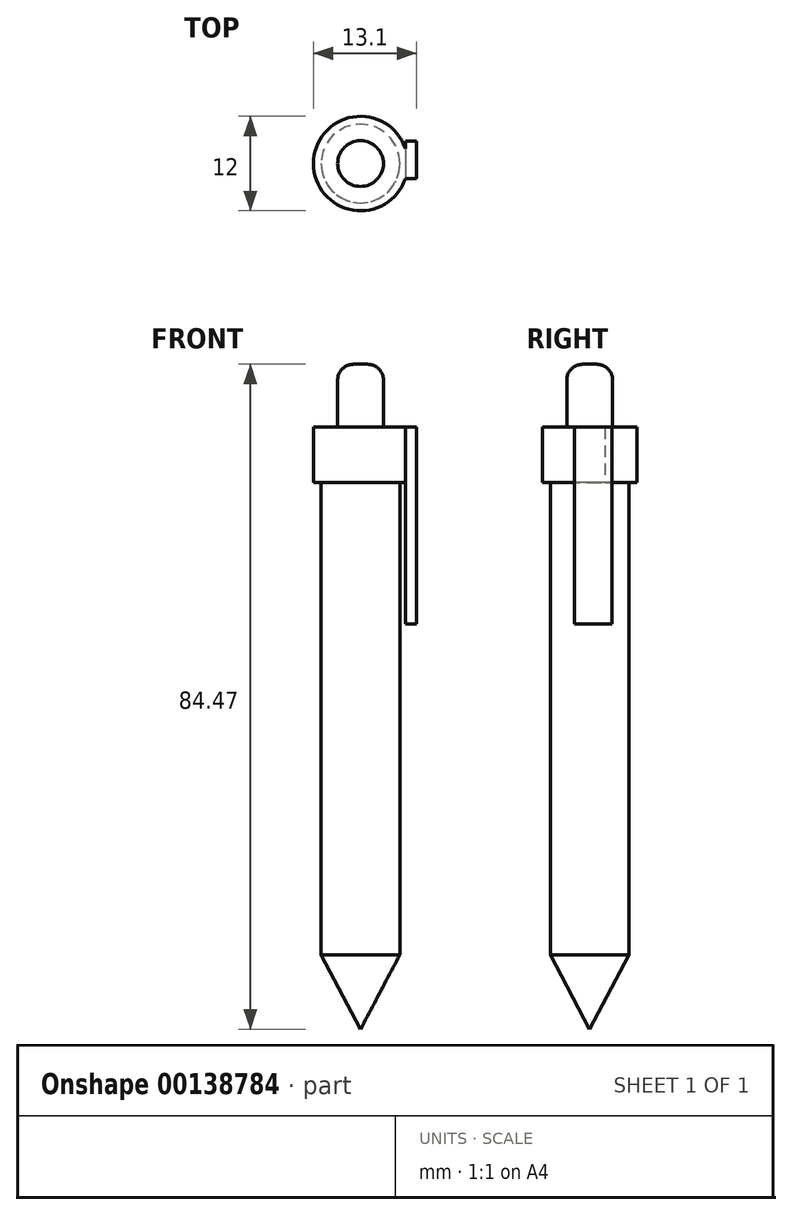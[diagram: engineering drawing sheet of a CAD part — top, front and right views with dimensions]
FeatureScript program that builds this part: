
annotation { "Feature Type Name" : "Feature", "Feature Type Description" : "" }
export const myFeature = defineFeature(function(context is Context, id is Id, definition is map)
    precondition{}
    {
        {
            var Q0;
            Q0=qCreatedBy(makeId("Top.planeOp"),FACE);
            var sketch = newSketch(context, id + "F0", { "sketchPlane" : qUnion([Q0])});
            skCircle(sketch, "E0", {"center": v(0, 0) * mm, "radius": 5 * mm});
            skSolve(sketch);
        }
        {
            var Q0;
            Q0 = qSketchRegion(id + "F0", true);
            extrude(context, id + "F1", {"entities" : qUnion([Q0]), "depth" : 60 * mm});
        }
        {
            var Q0;
            Q0=qCreatedBy(makeId("Right.planeOp"),FACE);
            var sketch = newSketch(context, id + "F2", { "sketchPlane" : qUnion([Q0])});
            skLineSegment(sketch, "E1", {"start": v(0, 0) * mm, "end": v(-5, 0) * mm});
            skLineSegment(sketch, "E2", {"start": v(-5, 0) * mm, "end": v(0, -9.47) * mm});
            skLineSegment(sketch, "E3", {"start": v(0, -9.47) * mm, "end": v(0, 0) * mm});
            skSolve(sketch);
        }
        {
            var Q0;
            Q0 = qSketchRegion(id + "F2", true);
            var Q1;
            Q1=sQuery(id+"F2.wireOp",EDGE,"E3");
            revolve(context, id + "F3", {"entities" : qUnion([Q0]), "axis" : qUnion([Q1]), "revolveType" : RevolveType.FULL});
        }
        {
            var Q0;
            Q0=makeQuery(id+"F1.opExtrude","CAP_FACE",FACE,{"disambiguationData":[OSD([sQuery(id+"F0.wireOp",EDGE,"E0")])],"isStart":false});
            var sketch = newSketch(context, id + "F4", { "sketchPlane" : qUnion([Q0])});
            skCircle(sketch, "E4", {"center": v(0, 0) * mm, "radius": 6 * mm});
            skSolve(sketch);
        }
        {
            var Q0;
            Q0 = qSketchRegion(id + "F4", true);
            extrude(context, id + "F5", {"entities" : qUnion([Q0]), "depth" : 7 * mm});
        }
        {
            var Q0;
            Q0=makeQuery(id+"F5.opExtrude","CAP_FACE",FACE,{"disambiguationData":[OSD([sQuery(id+"F4.wireOp",EDGE,"E4")])],"isStart":false});
            var sketch = newSketch(context, id + "F6", { "sketchPlane" : qUnion([Q0])});
            skLineSegment(sketch, "E5.bottom", {"start": v(7.1, 2.85) * mm, "end": v(5.68, 2.85) * mm});
            skLineSegment(sketch, "E5.top", {"start": v(7.1, -1.92) * mm, "end": v(5.68, -1.92) * mm});
            skLineSegment(sketch, "E5.left", {"start": v(7.1, 2.85) * mm, "end": v(7.1, -1.92) * mm});
            skLineSegment(sketch, "E5.right", {"start": v(5.68, 2.85) * mm, "end": v(5.68, -1.92) * mm});
            skSolve(sketch);
        }
        {
            var Q0;
            Q0 = qSketchRegion(id + "F6", true);
            extrude(context, id + "F7", {"entities" : qUnion([Q0]), "operationType" : NewBodyOperationType.ADD, "oppositeDirection" : true, "depth" : 25 * mm});
        }
        {
            var Q0;
            Q0=makeQuery(id+"F7.boolean.opBoolean","MERGE",FACE,{"derivedFrom":[makeQuery(id+"F5.opExtrude","CAP_FACE",FACE,{"disambiguationData":[OSD([sQuery(id+"F4.wireOp",EDGE,"E4")])],"isStart":false}),makeQuery(id+"F7.opExtrude","CAP_FACE",FACE,{"disambiguationData":[OSD([sQuery(id+"F6.wireOp",EDGE,"E5.bottom"),sQuery(id+"F6.wireOp",EDGE,"E5.top"),sQuery(id+"F6.wireOp",EDGE,"E5.left"),sQuery(id+"F6.wireOp",EDGE,"E5.right")])],"isStart":true})]});
            var sketch = newSketch(context, id + "F8", { "sketchPlane" : qUnion([Q0])});
            skCircle(sketch, "E6", {"center": v(0, 0) * mm, "radius": 2.9 * mm});
            skSolve(sketch);
        }
        {
            var Q0;
            Q0 = qSketchRegion(id + "F8", true);
            extrude(context, id + "F9", {"entities" : qUnion([Q0]), "depth" : 8 * mm});
        }
        {
            var Q0;
            Q0=makeQuery(id+"F9.opExtrude","CAP_EDGE",EDGE,{"disambiguationData":[OSD([sQuery(id+"F8.wireOp",EDGE,"E6")])],"isStart":false});
            fillet(context, id + "F10", {"entities" : qUnion([Q0]), "radius" : 2 * mm, "tangentPropagation" : true, "allowEdgeOverflow" : false});
        }
    });
